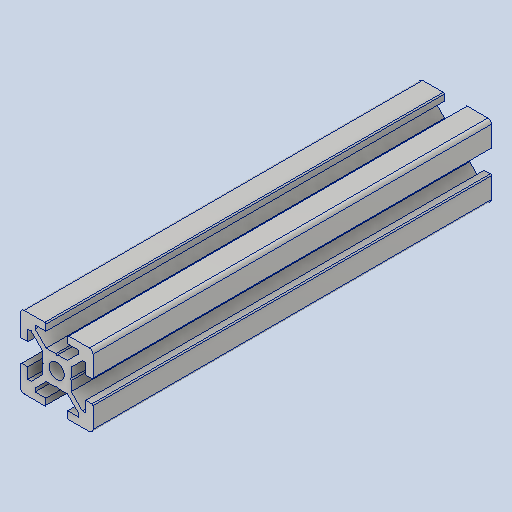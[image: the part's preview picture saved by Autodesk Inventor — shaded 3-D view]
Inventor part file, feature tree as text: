
AUTODESK INVENTOR PART (.ipt)
format: ipt  version: 2024 (Build 280153000, 153)  size: 335,872 bytes
history: native  units: mm
features: other x7, extrude x1, sketch x1
ambient origin geometry x8: Origin, YZ Plane, XZ Plane, XY Plane, X Axis, Y Axis, Z Axis, Center Point
bodies: Solid1 (feature_tree)
feature tree (9):
  extrude  "Extrusion1"  TaperAngle=0.0deg  [1 undecoded]
  other  "to_frame_XY"
  other  "to_frame_YZ"
  other  "to_frame_ZX"
  other  "to_frame_X"
  other  "to_frame_Y"
  other  "to_frame_Z"
  other  "to_frame_Center"
  sketch  "Sketch_5"  dims[d0=110.0mm d1=0.0mm d2=0.0mm]
note: 1 required parameter value undecoded (feature->parameter linkage not recoverable at this tier; creation-order binding heuristic only, values carry confidence <= 0.55)
